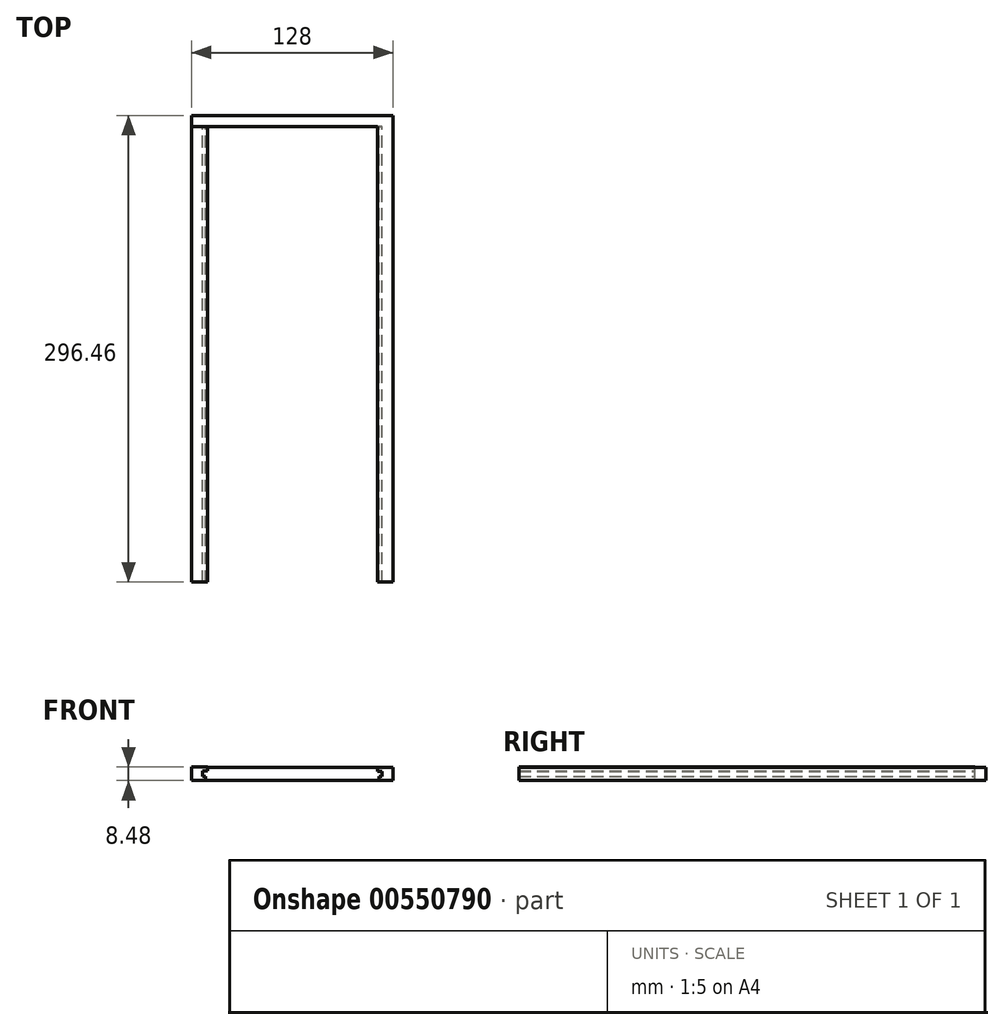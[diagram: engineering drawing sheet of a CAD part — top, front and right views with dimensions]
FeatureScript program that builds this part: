
annotation { "Feature Type Name" : "Feature", "Feature Type Description" : "" }
export const myFeature = defineFeature(function(context is Context, id is Id, definition is map)
    precondition{}
    {
        {
            var Q0;
            Q0=qCreatedBy(makeId("Front.planeOp"),FACE);
            var sketch = newSketch(context, id + "F0", { "sketchPlane" : qUnion([Q0])});
            skLineSegment(sketch, "E0", {"start": v(-57.44, 39) * mm, "end": v(-47.44, 39) * mm});
            skLineSegment(sketch, "E1", {"start": v(-47.44, 39) * mm, "end": v(-47.44, 30.6) * mm});
            skLineSegment(sketch, "E2", {"start": v(-47.44, 30.6) * mm, "end": v(-56.44, 30.6) * mm});
            skLineSegment(sketch, "E3", {"start": v(-56.44, 30.6) * mm, "end": v(-56.44, 33.1) * mm});
            skLineSegment(sketch, "E4", {"start": v(-56.44, 33.1) * mm, "end": v(-54.44, 33.1) * mm});
            skLineSegment(sketch, "E5", {"start": v(-54.44, 33.1) * mm, "end": v(-54.44, 36.5) * mm});
            skLineSegment(sketch, "E6", {"start": v(-54.44, 36.5) * mm, "end": v(-57.44, 36.5) * mm});
            skLineSegment(sketch, "E7", {"start": v(-57.44, 36.5) * mm, "end": v(-57.44, 39) * mm});
            skSolve(sketch);
        }
        {
            var Q0;
            Q0=qSketchRegion(id+"F0",true);
            extrude(context, id + "F1", {"entities" : qUnion([Q0]), "depth" : 289.46 * mm, "offsetDistance" : 25 * mm});
        }
        {
            var Q0;
            Q0=qCreatedBy(makeId("Front.planeOp"),FACE);
            var sketch = newSketch(context, id + "F2", { "sketchPlane" : qUnion([Q0])});
            skLineSegment(sketch, "E8.bottom", {"start": v(-175.44, 39) * mm, "end": v(-47.44, 39) * mm});
            skLineSegment(sketch, "E8.top", {"start": v(-175.44, 30.6) * mm, "end": v(-47.44, 30.6) * mm});
            skLineSegment(sketch, "E8.left", {"start": v(-175.44, 39) * mm, "end": v(-175.44, 30.6) * mm});
            skLineSegment(sketch, "E8.right", {"start": v(-47.44, 39) * mm, "end": v(-47.44, 30.6) * mm});
            skSolve(sketch);
        }
        {
            var Q0;
            Q0=makeQuery(id+"F2.imprint","IMPRINT",FACE,{"disambiguationData":[TD([[makeQuery(id+"F2.imprint","IMPRINT",EDGE,{"derivedFrom":sQuery(id+"F2.wireOp",EDGE,"E8.bottom")}),-1.0]])]});
            extrude(context, id + "F3", {"entities" : qUnion([Q0]), "operationType" : NewBodyOperationType.ADD, "oppositeDirection" : true, "depth" : 7 * mm, "offsetDistance" : 25 * mm});
        }
        {
            var Q0;
            Q0=qCreatedBy(makeId("Front.planeOp"),FACE);
            var sketch = newSketch(context, id + "F4", { "sketchPlane" : qUnion([Q0])});
            skLineSegment(sketch, "E9.MirrorCS", {"start": v(-165.44, 39.07) * mm, "end": v(-175.44, 39.07) * mm});
            skLineSegment(sketch, "E10.MirrorCS", {"start": v(-175.44, 39.07) * mm, "end": v(-175.44, 30.67) * mm});
            skLineSegment(sketch, "E11.MirrorCS", {"start": v(-175.44, 30.67) * mm, "end": v(-166.44, 30.67) * mm});
            skLineSegment(sketch, "E12.MirrorCS", {"start": v(-166.44, 30.67) * mm, "end": v(-166.44, 33.17) * mm});
            skLineSegment(sketch, "E13.MirrorCS", {"start": v(-166.44, 33.17) * mm, "end": v(-168.44, 33.17) * mm});
            skLineSegment(sketch, "E14.MirrorCS", {"start": v(-168.44, 33.17) * mm, "end": v(-168.44, 36.57) * mm});
            skLineSegment(sketch, "E15.MirrorCS", {"start": v(-168.44, 36.57) * mm, "end": v(-165.44, 36.57) * mm});
            skLineSegment(sketch, "E16.MirrorCS", {"start": v(-165.44, 36.57) * mm, "end": v(-165.44, 39.07) * mm});
            skSolve(sketch);
        }
        {
            var Q0;
            Q0=qSketchRegion(id+"F4",true);
            extrude(context, id + "F5", {"entities" : qUnion([Q0]), "operationType" : NewBodyOperationType.ADD, "depth" : 289.46 * mm, "offsetDistance" : 25 * mm});
        }
    });
